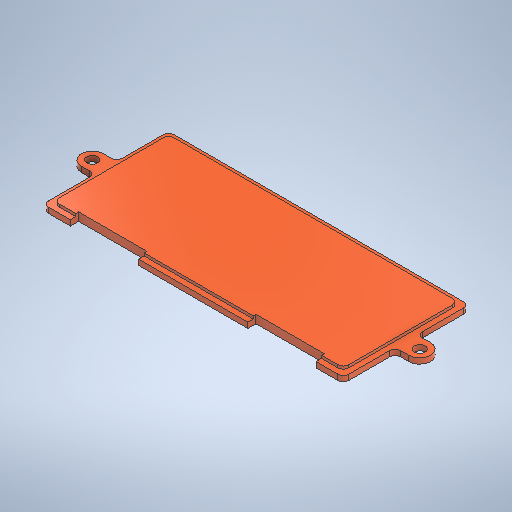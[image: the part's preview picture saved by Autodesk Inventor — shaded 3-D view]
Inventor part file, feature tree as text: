
AUTODESK INVENTOR PART (.ipt)
format: ipt  version: 2025 (Build 290162010, 162A)  size: 345,600 bytes
history: native  units: mm
features: extrude x3, sketch x3, plane x2, fillet x1
ambient origin geometry x8: Origin, YZ Plane, XZ Plane, XY Plane, X Axis, Y Axis, Z Axis, Center Point
bodies: Solid1 (feature_tree)
feature tree (9):
  extrude  "Extrusion1"  Depth=46.0mm
  extrude  "Extrusion2"  Depth=4.0mm
  fillet  "Fillet1"  Radius=4.0mm
  extrude  "Extrusion3"  Depth=8.0mm
  plane  "Work Plane1"
  plane  "Work Plane2"
  sketch  "Sketch1"  dims[d0=110.0mm d1=46.0mm]
  sketch  "Sketch2"  dims[d2=4.0mm d3=5.0mm d4=4.0mm]
  sketch  "Sketch3"  dims[d5=5.0mm d6=8.0mm d7=5.0mm d8=4.0mm d9=8.0mm d10=5.0mm d11=4.0mm d12=2.0mm d13=0.0mm d14=106.0mm d15=42.0mm d16=1.0mm d17=0.0mm d18=2.0mm d19=25.0mm d20=3.0mm d21=25.0mm d22=3.0mm d23=10.0mm d24=10.0mm d25=0.0mm d26=0.0mm]
